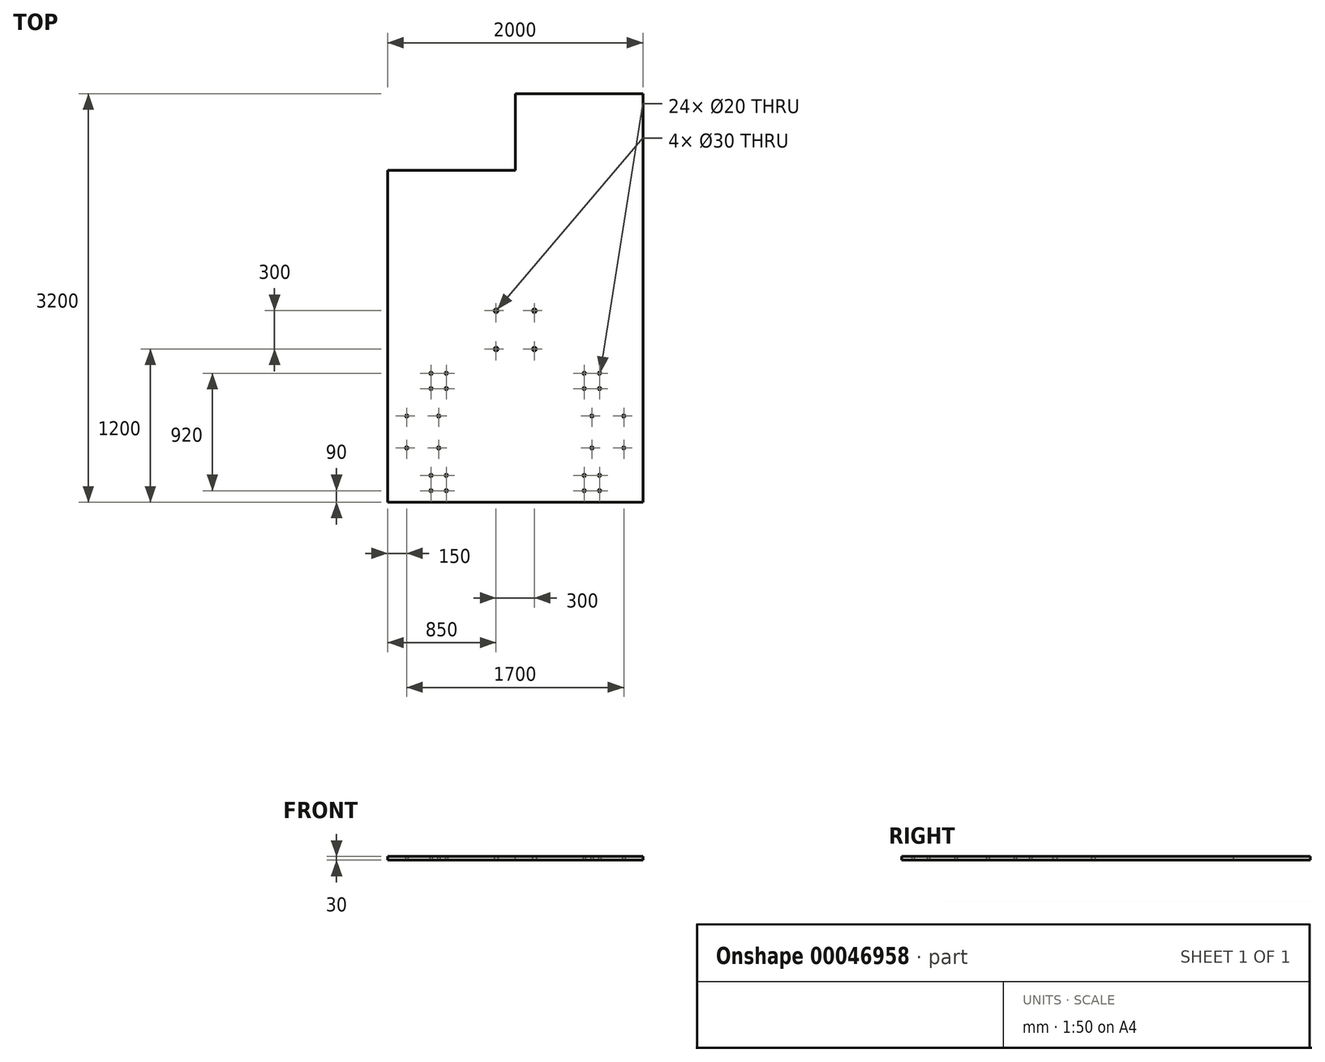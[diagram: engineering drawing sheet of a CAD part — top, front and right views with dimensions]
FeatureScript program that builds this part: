
annotation { "Feature Type Name" : "Feature", "Feature Type Description" : "" }
export const myFeature = defineFeature(function(context is Context, id is Id, definition is map)
    precondition{}
    {
        {
            var Q0;
            Q0=qCreatedBy(makeId("Top.planeOp"),FACE);
            var sketch = newSketch(context, id + "F0", { "sketchPlane" : qUnion([Q0])});
            skLineSegment(sketch, "E0.rect.bottom", {"start": v(-600, -400) * mm, "end": v(600, -400) * mm, "construction": true});
            skLineSegment(sketch, "E0.rect.top", {"start": v(-600, 400) * mm, "end": v(600, 400) * mm, "construction": true});
            skLineSegment(sketch, "E0.rect.left", {"start": v(-600, -400) * mm, "end": v(-600, 400) * mm, "construction": true});
            skLineSegment(sketch, "E0.rect.right", {"start": v(600, -400) * mm, "end": v(600, 400) * mm, "construction": true});
            skPoint(sketch, "E0.rect.middle", {"position": v(0, 0) * mm});
            skLineSegment(sketch, "E1.rect.bottom", {"start": v(-675, 325) * mm, "end": v(-525, 325) * mm, "construction": true});
            skLineSegment(sketch, "E1.rect.top", {"start": v(-675, 475) * mm, "end": v(-525, 475) * mm, "construction": true});
            skLineSegment(sketch, "E1.rect.left", {"start": v(-675, 325) * mm, "end": v(-675, 475) * mm, "construction": true});
            skLineSegment(sketch, "E1.rect.right", {"start": v(-525, 325) * mm, "end": v(-525, 475) * mm, "construction": true});
            skPoint(sketch, "E1.rect.middle", {"position": v(-600, 400) * mm});
            skLineSegment(sketch, "E2.rect.bottom", {"start": v(-660, 340) * mm, "end": v(-540, 340) * mm, "construction": true});
            skLineSegment(sketch, "E2.rect.top", {"start": v(-660, 460) * mm, "end": v(-540, 460) * mm, "construction": true});
            skLineSegment(sketch, "E2.rect.left", {"start": v(-660, 340) * mm, "end": v(-660, 460) * mm, "construction": true});
            skLineSegment(sketch, "E2.rect.right", {"start": v(-540, 340) * mm, "end": v(-540, 460) * mm, "construction": true});
            skCircle(sketch, "E3", {"center": v(-660, 460) * mm, "radius": 10 * mm});
            skCircle(sketch, "E4", {"center": v(-540, 460) * mm, "radius": 10 * mm});
            skCircle(sketch, "E5", {"center": v(-660, 340) * mm, "radius": 10 * mm});
            skCircle(sketch, "E6", {"center": v(-540, 340) * mm, "radius": 10 * mm});
            skCircle(sketch, "E7.MirrorC", {"center": v(660, 460) * mm, "radius": 10 * mm});
            skCircle(sketch, "E8.MirrorC", {"center": v(540, 460) * mm, "radius": 10 * mm});
            skCircle(sketch, "E9.MirrorC", {"center": v(660, 340) * mm, "radius": 10 * mm});
            skCircle(sketch, "E10.MirrorC", {"center": v(540, 340) * mm, "radius": 10 * mm});
            skPoint(sketch, "E11.MirrorP", {"position": v(600, 400) * mm});
            skLineSegment(sketch, "E12.MirrorCS", {"start": v(660, 340) * mm, "end": v(540, 340) * mm, "construction": true});
            skLineSegment(sketch, "E13.MirrorCS", {"start": v(675, 325) * mm, "end": v(525, 325) * mm, "construction": true});
            skLineSegment(sketch, "E14.MirrorCS", {"start": v(675, 475) * mm, "end": v(525, 475) * mm, "construction": true});
            skLineSegment(sketch, "E15.MirrorCS", {"start": v(660, 460) * mm, "end": v(540, 460) * mm, "construction": true});
            skLineSegment(sketch, "E16.MirrorCS", {"start": v(675, 325) * mm, "end": v(675, 475) * mm, "construction": true});
            skLineSegment(sketch, "E17.MirrorCS", {"start": v(525, 325) * mm, "end": v(525, 475) * mm, "construction": true});
            skLineSegment(sketch, "E18.MirrorCS", {"start": v(660, 340) * mm, "end": v(660, 460) * mm, "construction": true});
            skLineSegment(sketch, "E19.MirrorCS", {"start": v(540, 340) * mm, "end": v(540, 460) * mm, "construction": true});
            skCircle(sketch, "E20.MirrorC", {"center": v(660, -340) * mm, "radius": 10 * mm});
            skCircle(sketch, "E21.MirrorC", {"center": v(-660, -340) * mm, "radius": 10 * mm});
            skCircle(sketch, "E22.MirrorC", {"center": v(-540, -460) * mm, "radius": 10 * mm});
            skCircle(sketch, "E23.MirrorC", {"center": v(540, -460) * mm, "radius": 10 * mm});
            skCircle(sketch, "E24.MirrorC", {"center": v(-660, -460) * mm, "radius": 10 * mm});
            skCircle(sketch, "E25.MirrorC", {"center": v(540, -340) * mm, "radius": 10 * mm});
            skCircle(sketch, "E26.MirrorC", {"center": v(-540, -340) * mm, "radius": 10 * mm});
            skCircle(sketch, "E27.MirrorC", {"center": v(660, -460) * mm, "radius": 10 * mm});
            skPoint(sketch, "E28.MirrorP", {"position": v(600, -400) * mm});
            skPoint(sketch, "E29.MirrorP", {"position": v(-600, -400) * mm});
            skLineSegment(sketch, "E30.MirrorCS", {"start": v(-675, -325) * mm, "end": v(-525, -325) * mm, "construction": true});
            skLineSegment(sketch, "E31.MirrorCS", {"start": v(675, -325) * mm, "end": v(525, -325) * mm, "construction": true});
            skLineSegment(sketch, "E32.MirrorCS", {"start": v(675, -325) * mm, "end": v(675, -475) * mm, "construction": true});
            skLineSegment(sketch, "E33.MirrorCS", {"start": v(660, -340) * mm, "end": v(660, -460) * mm, "construction": true});
            skLineSegment(sketch, "E34.MirrorCS", {"start": v(660, -340) * mm, "end": v(540, -340) * mm, "construction": true});
            skLineSegment(sketch, "E35.MirrorCS", {"start": v(675, -475) * mm, "end": v(525, -475) * mm, "construction": true});
            skLineSegment(sketch, "E36.MirrorCS", {"start": v(660, -460) * mm, "end": v(540, -460) * mm, "construction": true});
            skLineSegment(sketch, "E37.MirrorCS", {"start": v(525, -325) * mm, "end": v(525, -475) * mm, "construction": true});
            skLineSegment(sketch, "E38.MirrorCS", {"start": v(540, -340) * mm, "end": v(540, -460) * mm, "construction": true});
            skLineSegment(sketch, "E39.MirrorCS", {"start": v(-525, -325) * mm, "end": v(-525, -475) * mm, "construction": true});
            skLineSegment(sketch, "E40.MirrorCS", {"start": v(-675, -475) * mm, "end": v(-525, -475) * mm, "construction": true});
            skLineSegment(sketch, "E41.MirrorCS", {"start": v(-540, -340) * mm, "end": v(-540, -460) * mm, "construction": true});
            skLineSegment(sketch, "E42.MirrorCS", {"start": v(-660, -340) * mm, "end": v(-660, -460) * mm, "construction": true});
            skLineSegment(sketch, "E43.MirrorCS", {"start": v(-660, -460) * mm, "end": v(-540, -460) * mm, "construction": true});
            skLineSegment(sketch, "E44.MirrorCS", {"start": v(-660, -340) * mm, "end": v(-540, -340) * mm, "construction": true});
            skLineSegment(sketch, "E45.MirrorCS", {"start": v(-675, -325) * mm, "end": v(-675, -475) * mm, "construction": true});
            skLineSegment(sketch, "E46", {"start": v(0, 0) * mm, "end": v(0, 800) * mm, "construction": true});
            skLineSegment(sketch, "E47.rect.bottom", {"start": v(150, 650) * mm, "end": v(-150, 650) * mm, "construction": true});
            skLineSegment(sketch, "E47.rect.top", {"start": v(150, 950) * mm, "end": v(-150, 950) * mm, "construction": true});
            skLineSegment(sketch, "E47.rect.left", {"start": v(150, 650) * mm, "end": v(150, 950) * mm, "construction": true});
            skLineSegment(sketch, "E47.rect.right", {"start": v(-150, 650) * mm, "end": v(-150, 950) * mm, "construction": true});
            skPoint(sketch, "E47.rect.middle", {"position": v(0, 800) * mm});
            skCircle(sketch, "E48", {"center": v(-150, 950) * mm, "radius": 15 * mm});
            skCircle(sketch, "E49", {"center": v(150, 950) * mm, "radius": 15 * mm});
            skCircle(sketch, "E50", {"center": v(150, 650) * mm, "radius": 15 * mm});
            skCircle(sketch, "E51", {"center": v(-150, 650) * mm, "radius": 15 * mm});
            skLineSegment(sketch, "E52.rect.bottom", {"start": v(1000, -550) * mm, "end": v(-1000, -550) * mm});
            skLineSegment(sketch, "E53.top", {"start": v(-1000, 2650) * mm, "end": v(1000, 2650) * mm});
            skLineSegment(sketch, "E54", {"start": v(-1000, 2650) * mm, "end": v(-1000, -550) * mm});
            skLineSegment(sketch, "E55", {"start": v(1000, 2650) * mm, "end": v(1000, -550) * mm});
            skLineSegment(sketch, "E56.bottom", {"start": v(-850, 125) * mm, "end": v(-600, 125) * mm, "construction": true});
            skLineSegment(sketch, "E56.top", {"start": v(-850, -125) * mm, "end": v(-600, -125) * mm, "construction": true});
            skLineSegment(sketch, "E56.left", {"start": v(-850, 125) * mm, "end": v(-850, -125) * mm, "construction": true});
            skLineSegment(sketch, "E56.right", {"start": v(-600, 125) * mm, "end": v(-600, -125) * mm, "construction": true});
            skCircle(sketch, "E57", {"center": v(-600, 125) * mm, "radius": 10 * mm});
            skCircle(sketch, "E58", {"center": v(-850, 125) * mm, "radius": 10 * mm});
            skCircle(sketch, "E59", {"center": v(-850, -125) * mm, "radius": 10 * mm});
            skCircle(sketch, "E60", {"center": v(-600, -125) * mm, "radius": 10 * mm});
            skCircle(sketch, "E61.MirrorC", {"center": v(850, -125) * mm, "radius": 10 * mm});
            skCircle(sketch, "E62.MirrorC", {"center": v(850, 125) * mm, "radius": 10 * mm});
            skCircle(sketch, "E63.MirrorC", {"center": v(600, 125) * mm, "radius": 10 * mm});
            skCircle(sketch, "E64.MirrorC", {"center": v(600, -125) * mm, "radius": 10 * mm});
            skLineSegment(sketch, "E65.MirrorCS", {"start": v(850, 125) * mm, "end": v(850, -125) * mm, "construction": true});
            skLineSegment(sketch, "E66.MirrorCS", {"start": v(850, 125) * mm, "end": v(600, 125) * mm, "construction": true});
            skLineSegment(sketch, "E67.MirrorCS", {"start": v(600, 125) * mm, "end": v(600, -125) * mm, "construction": true});
            skLineSegment(sketch, "E68.MirrorCS", {"start": v(850, -125) * mm, "end": v(600, -125) * mm, "construction": true});
            skLineSegment(sketch, "E69", {"start": v(-600, 125) * mm, "end": v(-850, -125) * mm, "construction": true});
            skLineSegment(sketch, "E70", {"start": v(-600, -125) * mm, "end": v(-850, 125) * mm, "construction": true});
            skPoint(sketch, "E71", {"position": v(-725, 0) * mm});
            skSolve(sketch);
        }
        {
            var Q0;
            Q0=qSketchRegion(id+"F0",true);
            extrude(context, id + "F1", {"entities" : qUnion([Q0]), "depth" : 30 * mm});
        }
        {
            var Q0;
            Q0=makeQuery(id+"F1.opExtrude","CAP_FACE",FACE,{"disambiguationData":[OSD([sQuery(id+"F0.wireOp",EDGE,"E3"),sQuery(id+"F0.wireOp",EDGE,"E4"),sQuery(id+"F0.wireOp",EDGE,"E5"),sQuery(id+"F0.wireOp",EDGE,"E6"),sQuery(id+"F0.wireOp",EDGE,"E7.MirrorC"),sQuery(id+"F0.wireOp",EDGE,"E8.MirrorC"),sQuery(id+"F0.wireOp",EDGE,"E9.MirrorC"),sQuery(id+"F0.wireOp",EDGE,"E10.MirrorC"),sQuery(id+"F0.wireOp",EDGE,"E20.MirrorC"),sQuery(id+"F0.wireOp",EDGE,"E21.MirrorC"),sQuery(id+"F0.wireOp",EDGE,"E22.MirrorC"),sQuery(id+"F0.wireOp",EDGE,"E23.MirrorC"),sQuery(id+"F0.wireOp",EDGE,"E24.MirrorC"),sQuery(id+"F0.wireOp",EDGE,"E25.MirrorC"),sQuery(id+"F0.wireOp",EDGE,"E26.MirrorC"),sQuery(id+"F0.wireOp",EDGE,"E27.MirrorC"),sQuery(id+"F0.wireOp",EDGE,"E48"),sQuery(id+"F0.wireOp",EDGE,"E49"),sQuery(id+"F0.wireOp",EDGE,"E50"),sQuery(id+"F0.wireOp",EDGE,"E51"),sQuery(id+"F0.wireOp",EDGE,"E52.rect.bottom"),sQuery(id+"F0.wireOp",EDGE,"E53.top"),sQuery(id+"F0.wireOp",EDGE,"E54"),sQuery(id+"F0.wireOp",EDGE,"E55")])],"isStart":false});
            var sketch = newSketch(context, id + "F2", { "sketchPlane" : qUnion([Q0])});
            skLineSegment(sketch, "E72.bottom", {"start": v(-1000, 2650) * mm, "end": v(0, 2650) * mm});
            skLineSegment(sketch, "E72.top", {"start": v(-1000, 2050) * mm, "end": v(0, 2050) * mm});
            skLineSegment(sketch, "E72.left", {"start": v(-1000, 2650) * mm, "end": v(-1000, 2050) * mm});
            skLineSegment(sketch, "E72.right", {"start": v(0, 2650) * mm, "end": v(0, 2050) * mm});
            skSolve(sketch);
        }
        {
            var Q0;
            Q0 = qSketchRegion(id + "F2", true);
            extrude(context, id + "F3", {"entities" : qUnion([Q0]), "operationType" : NewBodyOperationType.REMOVE, "oppositeDirection" : true, "depth" : 30 * mm});
        }
    });
